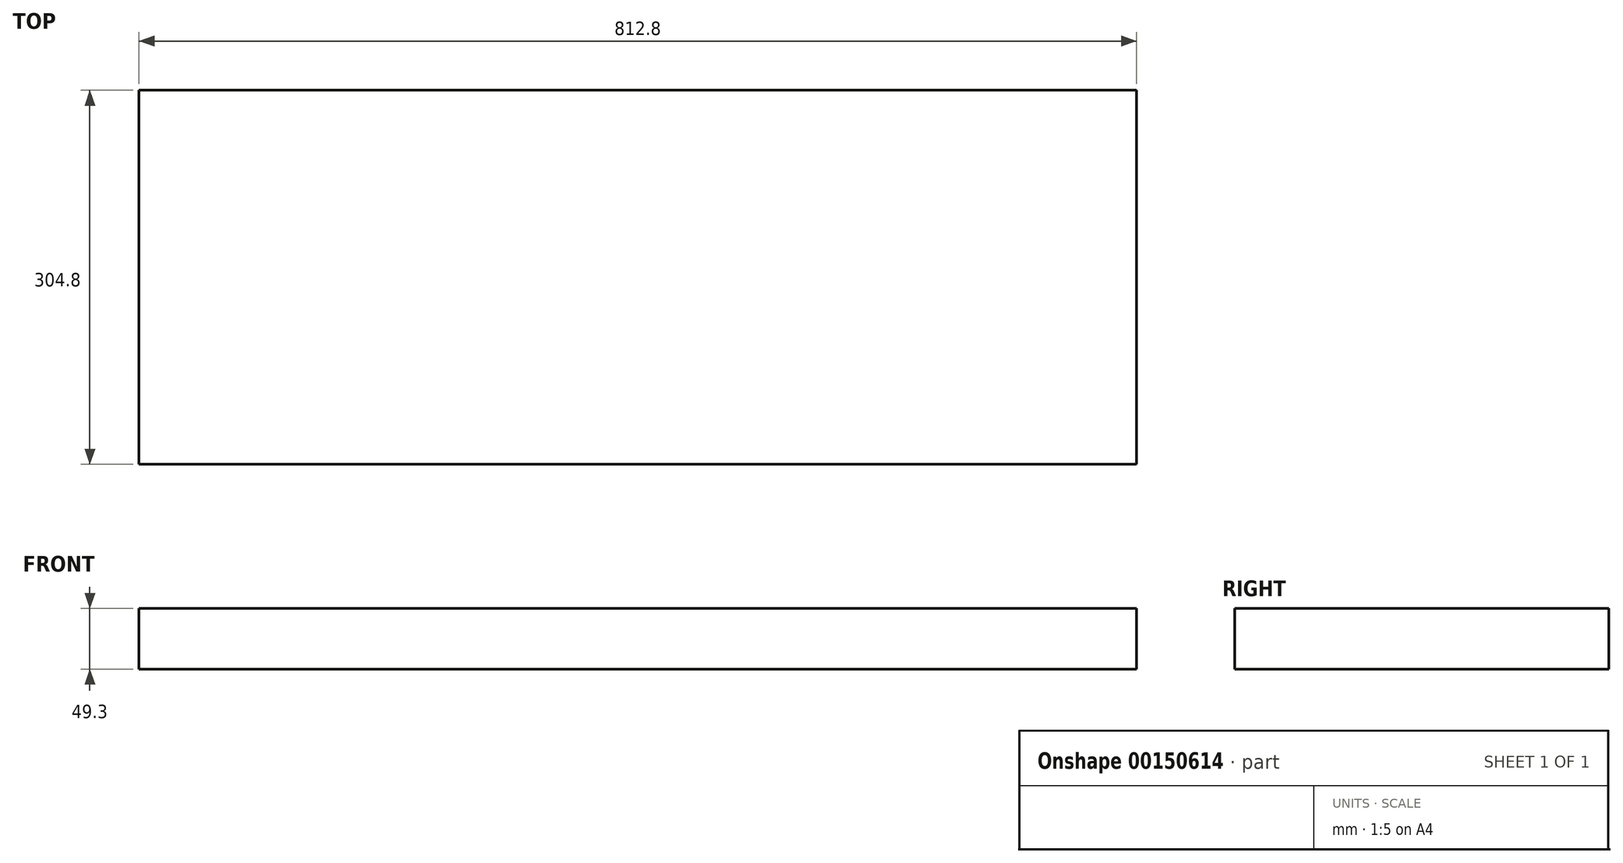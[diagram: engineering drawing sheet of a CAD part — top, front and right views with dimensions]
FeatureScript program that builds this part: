
annotation { "Feature Type Name" : "Feature", "Feature Type Description" : "" }
export const myFeature = defineFeature(function(context is Context, id is Id, definition is map)
    precondition{}
    {
        {
            var Q0;
            Q0=qCreatedBy(makeId("Front.planeOp"),FACE);
            var sketch = newSketch(context, id + "F0", { "sketchPlane" : qUnion([Q0])});
            skLineSegment(sketch, "E0.bottom", {"start": v(-401.75, -31.63) * mm, "end": v(411.05, -31.63) * mm});
            skLineSegment(sketch, "E0.top", {"start": v(-401.75, 17.67) * mm, "end": v(411.05, 17.67) * mm});
            skLineSegment(sketch, "E0.left", {"start": v(-401.75, -31.63) * mm, "end": v(-401.75, 17.67) * mm});
            skLineSegment(sketch, "E0.right", {"start": v(411.05, -31.63) * mm, "end": v(411.05, 17.67) * mm});
            skSolve(sketch);
        }
        {
            var Q0;
            Q0 = qSketchRegion(id + "F0", true);
            extrude(context, id + "F1", {"entities" : qUnion([Q0]), "depth" : 304.8 * mm});
        }
    });
